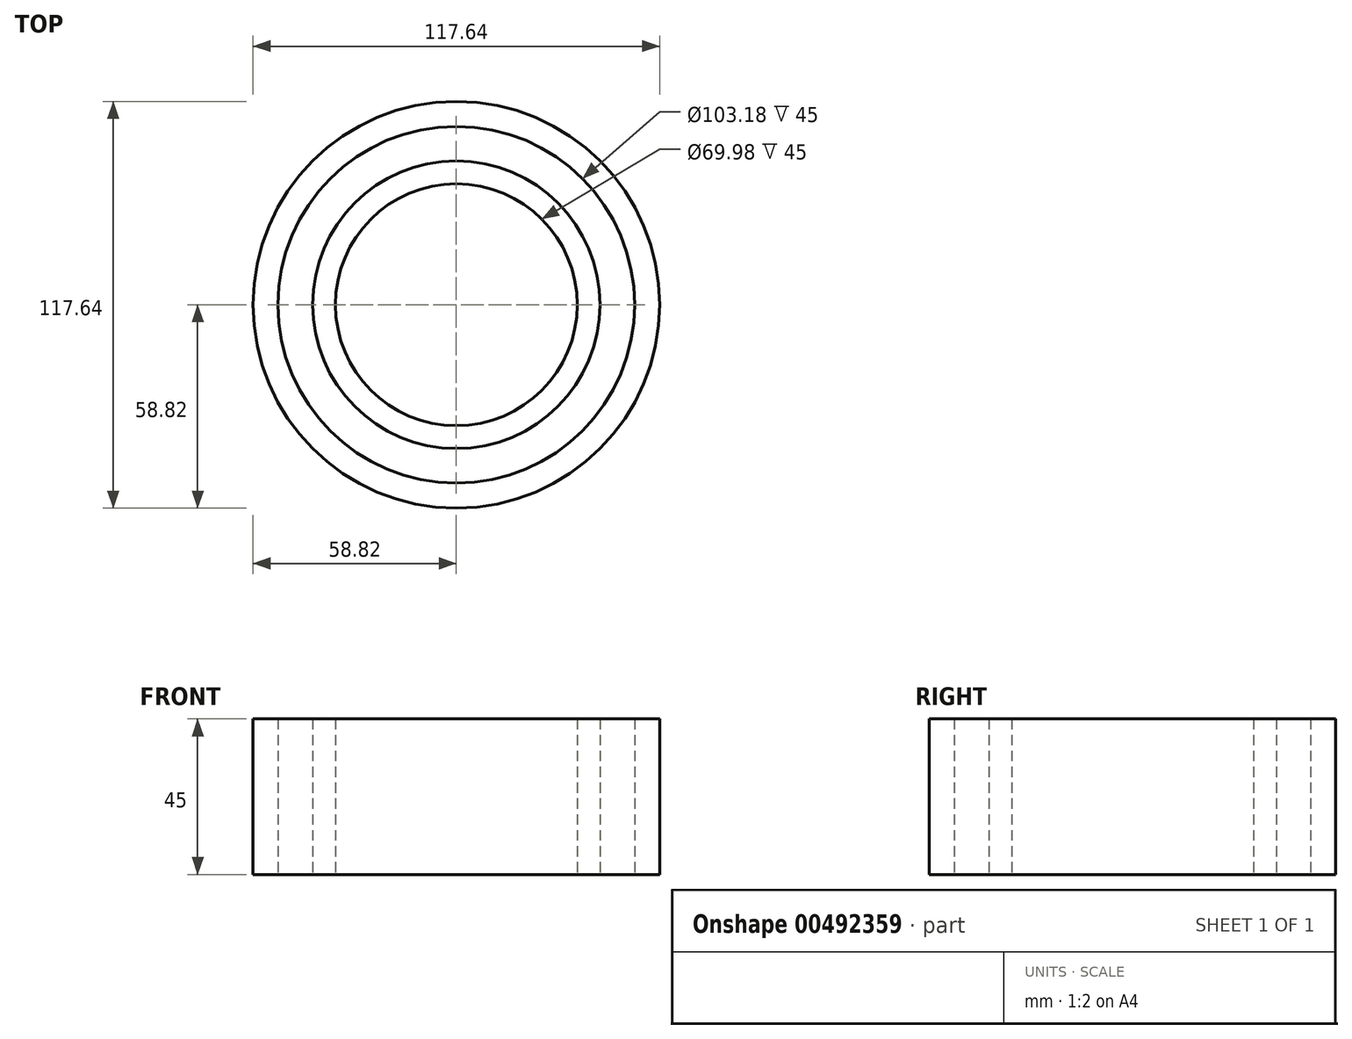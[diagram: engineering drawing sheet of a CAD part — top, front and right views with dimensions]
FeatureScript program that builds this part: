
annotation { "Feature Type Name" : "Feature", "Feature Type Description" : "" }
export const myFeature = defineFeature(function(context is Context, id is Id, definition is map)
    precondition{}
    {
        {
            var Q0;
            Q0=qCreatedBy(makeId("Top.planeOp"),FACE);
            var sketch = newSketch(context, id + "F0", { "sketchPlane" : qUnion([Q0])});
            skCircle(sketch, "E0", {"center": v(0, 0) * mm, "radius": 58.82 * mm});
            skCircle(sketch, "E1", {"center": v(0, 0) * mm, "radius": 51.59 * mm});
            skCircle(sketch, "E2.0", {"center": v(0, 0) * mm, "radius": 41.59 * mm});
            skCircle(sketch, "E3.0", {"center": v(0, 0) * mm, "radius": 34.99 * mm});
            skSolve(sketch);
        }
        {
            var Q0;
            Q0=makeQuery(id+"F0.imprint","IMPRINT",FACE,{"disambiguationData":[TD([[makeQuery(id+"F0.imprint","IMPRINT",EDGE,{"derivedFrom":sQuery(id+"F0.wireOp",EDGE,"E0")}),1.0]])]});
            var Q1;
            Q1=makeQuery(id+"F0.imprint","IMPRINT",FACE,{"disambiguationData":[TD([[makeQuery(id+"F0.imprint","IMPRINT",EDGE,{"derivedFrom":sQuery(id+"F0.wireOp",EDGE,"E2.0")}),1.0]])]});
            var Q2;
            Q2=sQuery(id+"F0.wireOp",EDGE,"E0");
            var Q3;
            Q3=sQuery(id+"F0.wireOp",EDGE,"E1");
            extrude(context, id + "F1", {"entities" : qUnion([Q0, Q1]), "surfaceEntities" : qUnion([Q2, Q3]), "depth" : 45 * mm});
        }
    });
